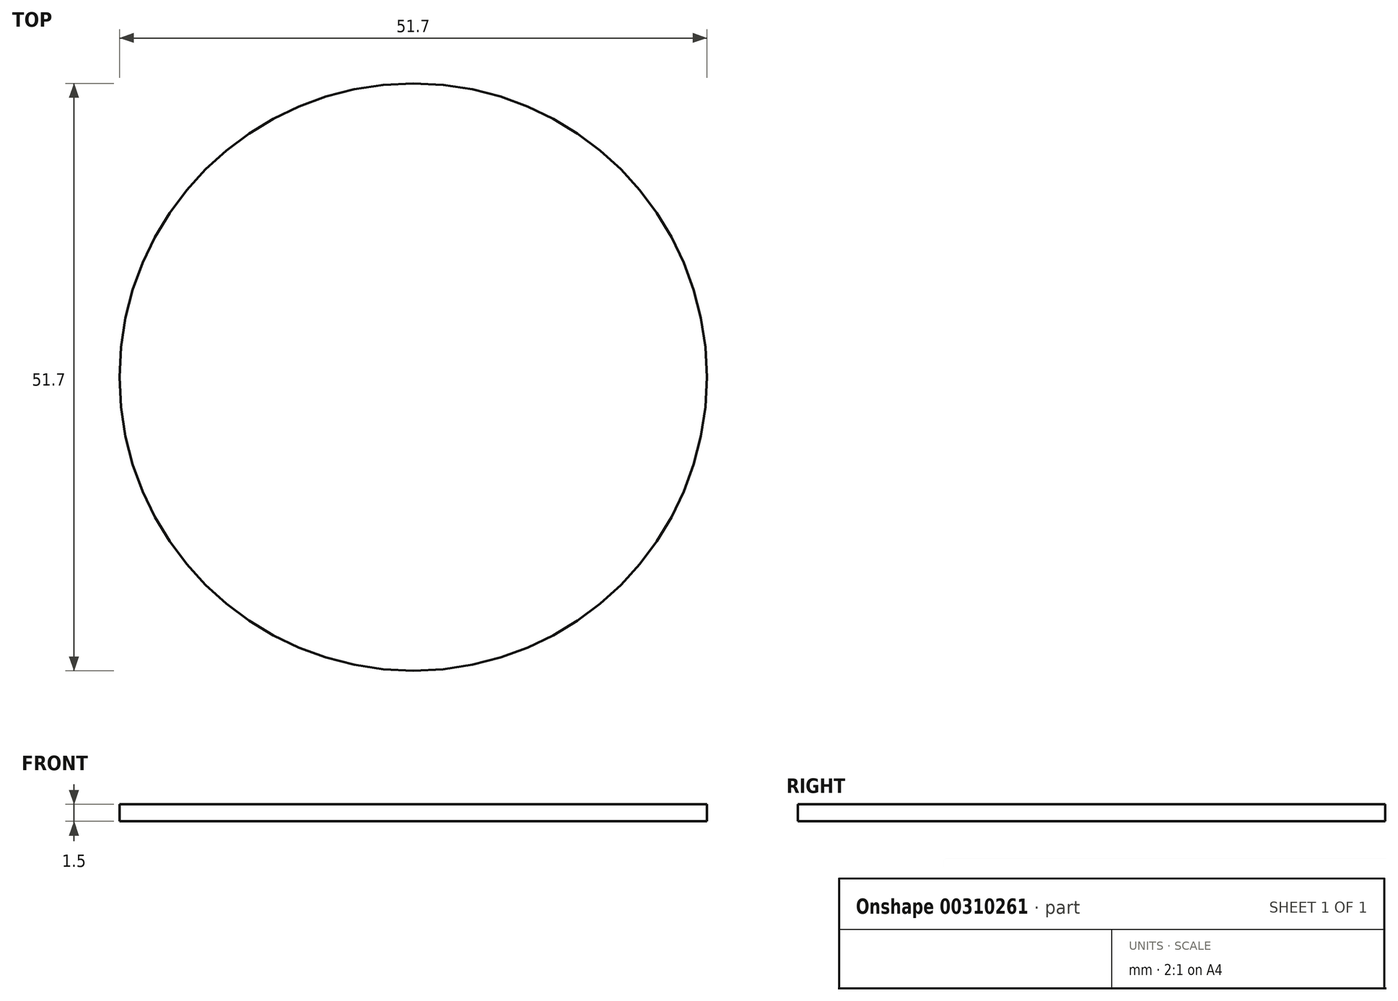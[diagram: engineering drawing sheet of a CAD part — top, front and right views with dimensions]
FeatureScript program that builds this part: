
annotation { "Feature Type Name" : "Feature", "Feature Type Description" : "" }
export const myFeature = defineFeature(function(context is Context, id is Id, definition is map)
    precondition{}
    {
        {
            var Q0;
            Q0=qCreatedBy(makeId("Front.planeOp"),FACE);
            var sketch = newSketch(context, id + "F0", { "sketchPlane" : qUnion([Q0])});
            skLineSegment(sketch, "E0", {"start": v(26, 39.5) * mm, "end": v(26, -55) * mm, "construction": true});
            skLineSegment(sketch, "E1", {"start": v(0, 39.5) * mm, "end": v(0, 38) * mm, "construction": true});
            skLineSegment(sketch, "E2", {"start": v(0, 39.5) * mm, "end": v(26, 39.5) * mm});
            skLineSegment(sketch, "E3", {"start": v(0, 38) * mm, "end": v(26, 38) * mm});
            skLineSegment(sketch, "E4", {"start": v(26, 38) * mm, "end": v(26, 39.5) * mm});
            skLineSegment(sketch, "E5", {"start": v(0, 39.5) * mm, "end": v(0.15, 39.5) * mm});
            skLineSegment(sketch, "E6", {"start": v(0.15, 39.5) * mm, "end": v(0.15, 38) * mm});
            skSolve(sketch);
        }
        {
            var Q0;
            Q0=makeQuery(id+"F0.imprint","IMPRINT",FACE,{"disambiguationData":[TD([[makeQuery(id+"F0.imprint","IMPRINT",EDGE,{"derivedFrom":sQuery(id+"F0.wireOp",EDGE,"E2")}),-1.0]])]});
            var Q1;
            Q1=sQuery(id+"F0.wireOp",EDGE,"E0");
            revolve(context, id + "F1", {"entities" : qUnion([Q0]), "axis" : qUnion([Q1]), "revolveType" : RevolveType.FULL});
        }
    });
